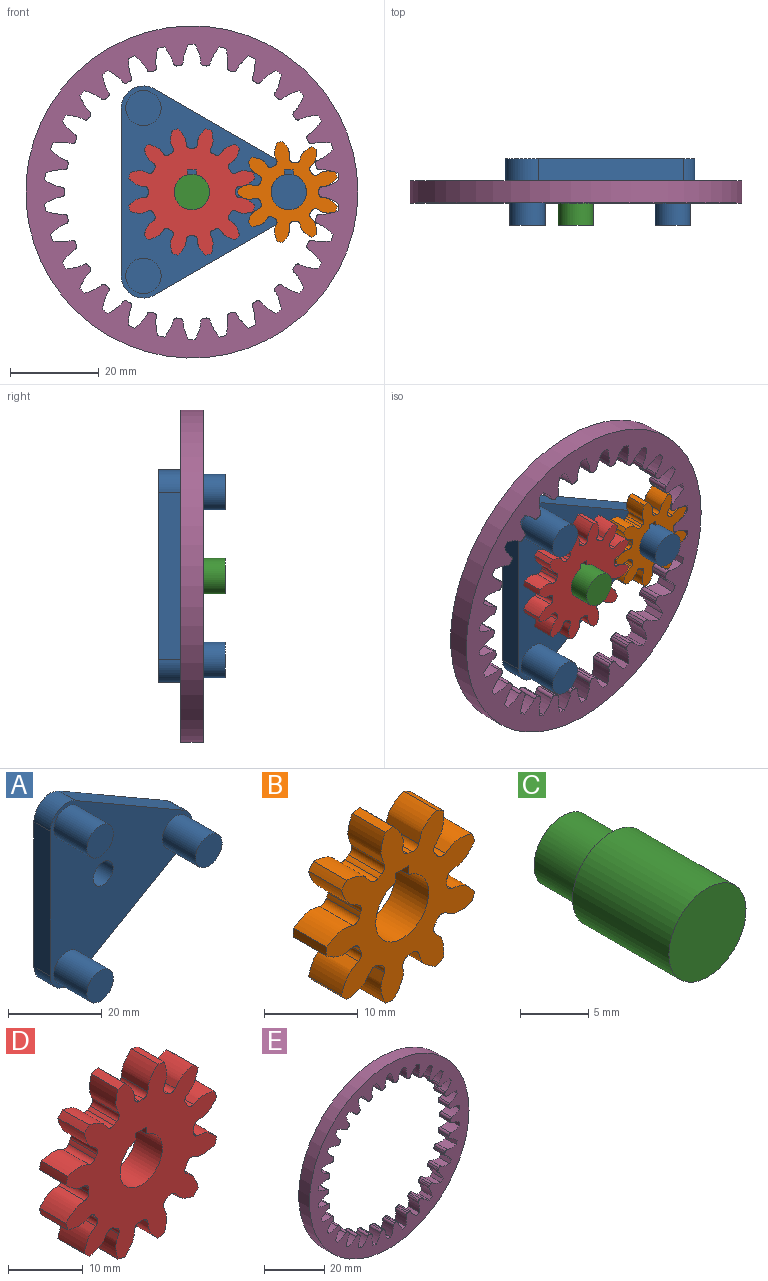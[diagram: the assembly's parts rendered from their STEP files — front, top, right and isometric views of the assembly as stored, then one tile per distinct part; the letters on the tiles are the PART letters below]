
ASSEMBLY  parts=5 mates=3
PART A: 15 faces, bbox 42.8x15x47.9 mm
  f0: cylinder r=5mm len=8.66mm, axis (0,-1,0), area 52.4mm2, adj f1,f5,f6,f7
  f1: plane 32.81x18.94mm, normal (0.5,0,0.87), area 189.4mm2, adj f0,f2,f6,f7
  f2: cylinder r=5mm len=7.5mm, axis (0,-1,0), area 52.4mm2, adj f1,f3,f6,f7
  f3: plane 37.89x5mm, normal (-1,0,0), area 189.4mm2, adj f2,f4,f6,f7
  f4: cylinder r=5mm len=7.5mm, axis (0,-1,0), area 52.4mm2, adj f3,f5,f6,f7
  f5: plane 32.81x18.94mm, normal (0.5,0,-0.87), area 189.4mm2, adj f0,f4,f6,f7
  f6: plane 47.89x42.81mm, normal (0,1,0), area 1240.2mm2, adj f0,f1,f2,f3,f4,f5,f14
  f7: plane 47.89x42.81mm, normal (0,-1,0), area 1089.4mm2, adj f0,f1,f2,f3,f4,f5,f8,f10
  f8: cylinder r=4mm len=10mm, axis (0,1,0), area 251.3mm2, adj f7,f9
  f9: plane 8x8mm, normal (0,-1,0), area 50.3mm2, adj f8
  f10: cylinder r=4mm len=10mm, axis (0,1,0), area 251.3mm2, adj f7,f11
  f11: plane 8x8mm, normal (0,-1,0), area 50.3mm2, adj f10
  f12: cylinder r=4mm len=10mm, axis (0,1,0), area 251.3mm2, adj f7,f13
  f13: plane 8x8mm, normal (0,-1,0), area 50.3mm2, adj f12
  f14: cylinder r=3mm len=6mm, axis (0,1,0), area 94.2mm2, adj f6,f7
PART B: 60 faces, bbox 22.5x5x22.8 mm
  f0: cylinder r=11.46mm len=5mm, axis (0,1,0), area 5.9mm2, adj f8,f14,f40,f57
  f1: cylinder r=11.46mm len=5mm, axis (0,1,0), area 5.9mm2, adj f8,f14,f52,f55
  f2: cylinder r=11.46mm len=5mm, axis (0,1,0), area 5.9mm2, adj f8,f14,f30,f47
  f3: cylinder r=11.46mm len=5mm, axis (0,1,0), area 5.9mm2, adj f8,f14,f42,f45
  f4: cylinder r=11.46mm len=5mm, axis (0,1,0), area 5.9mm2, adj f8,f14,f20,f37
  f5: cylinder r=11.46mm len=5mm, axis (0,1,0), area 5.9mm2, adj f8,f14,f32,f35
  f6: cylinder r=11.46mm len=5mm, axis (0,1,0), area 5.9mm2, adj f8,f14,f15,f27
  f7: cylinder r=11.46mm len=5mm, axis (0,1,0), area 5.9mm2, adj f8,f14,f22,f25
  f8: plane 22.83x22.49mm, normal (0,-1,0), area 210.7mm2, adj f0,f1,f2,f3,f4,f5,f6,f7
  f9: plane 5x1.13mm, normal (-1,0,0), area 5.6mm2, adj f8,f10,f12,f14
  f10: cylinder r=4mm len=8mm, axis (0,1,0), area 115.6mm2, adj f8,f9,f11,f14
  f11: plane 5x1.13mm, normal (1,0,0), area 5.6mm2, adj f8,f10,f12,f14
  f12: plane 5x2mm, normal (0,0,-1), area 10mm2, adj f8,f9,f11,f14
  f13: cylinder r=11.46mm len=5mm, axis (0,1,0), area 5.9mm2, adj f8,f14,f17,f50
  f14: plane 22.83x22.49mm, normal (0,1,0), area 210.7mm2, adj f0,f1,f2,f3,f4,f5,f6,f7
  f15: extruded ~5x3.47mm, area 21.3mm2, adj f6,f8,f14,f18
  f16: cylinder r=6.77mm len=5mm, axis (0,1,0), area 3.2mm2, adj f8,f14,f18,f19
  f17: extruded ~5x3.47mm, area 21.3mm2, adj f8,f13,f14,f19
  f18: cylinder r=0.85mm len=5mm, axis (0,1,0), area 6.2mm2, adj f8,f14,f15,f16
  f19: cylinder r=0.85mm len=5mm, axis (0,1,0), area 6.2mm2, adj f8,f14,f16,f17
  f20: extruded ~5x3.8mm, area 21.3mm2, adj f4,f8,f14,f23
  f21: cylinder r=6.77mm len=5mm, axis (0,1,0), area 3.2mm2, adj f8,f14,f23,f24
  f22: extruded ~5x3.05mm, area 21.3mm2, adj f7,f8,f14,f24
  f23: cylinder r=0.85mm len=5mm, axis (0,1,0), area 6.2mm2, adj f8,f14,f20,f21
  f24: cylinder r=0.85mm len=5mm, axis (0,1,0), area 6.2mm2, adj f8,f14,f21,f22
  f25: extruded ~5x3.89mm, area 21.3mm2, adj f7,f8,f14,f28
  f26: cylinder r=6.77mm len=5mm, axis (0,1,0), area 3.2mm2, adj f8,f14,f28,f29
  f27: extruded ~5x4.05mm, area 21.3mm2, adj f6,f8,f14,f29
  f28: cylinder r=0.85mm len=5mm, axis (0,1,0), area 6.2mm2, adj f8,f14,f25,f26
  f29: cylinder r=0.85mm len=5mm, axis (0,1,0), area 6.2mm2, adj f8,f14,f26,f27
  f30: extruded ~5x4mm, area 21.3mm2, adj f2,f8,f14,f33
  f31: cylinder r=6.77mm len=5mm, axis (0,1,0), area 3.2mm2, adj f8,f14,f33,f34
  f32: extruded ~5x3.22mm, area 21.3mm2, adj f5,f8,f14,f34
  f33: cylinder r=0.85mm len=5mm, axis (0,1,0), area 6.2mm2, adj f8,f14,f30,f31
  f34: cylinder r=0.85mm len=5mm, axis (0,1,0), area 6.2mm2, adj f8,f14,f31,f32
  f35: extruded ~5x3.61mm, area 21.3mm2, adj f5,f8,f14,f38
  f36: cylinder r=6.77mm len=5mm, axis (0,1,0), area 3.2mm2, adj f8,f14,f38,f39
  f37: extruded ~5x4.09mm, area 21.3mm2, adj f4,f8,f14,f39
  f38: cylinder r=0.85mm len=5mm, axis (0,1,0), area 6.2mm2, adj f8,f14,f35,f36
  f39: cylinder r=0.85mm len=5mm, axis (0,1,0), area 6.2mm2, adj f8,f14,f36,f37
  f40: extruded ~5x4.09mm, area 21.3mm2, adj f0,f8,f14,f43
  f41: cylinder r=6.77mm len=5mm, axis (0,1,0), area 3.2mm2, adj f8,f14,f43,f44
  f42: extruded ~5x3.61mm, area 21.3mm2, adj f3,f8,f14,f44
  f43: cylinder r=0.85mm len=5mm, axis (0,1,0), area 6.2mm2, adj f8,f14,f40,f41
  f44: cylinder r=0.85mm len=5mm, axis (0,1,0), area 6.2mm2, adj f8,f14,f41,f42
  f45: extruded ~5x3.22mm, area 21.3mm2, adj f3,f8,f14,f48
  f46: cylinder r=6.77mm len=5mm, axis (0,1,0), area 3.2mm2, adj f8,f14,f48,f49
  f47: extruded ~5x4mm, area 21.3mm2, adj f2,f8,f14,f49
  f48: cylinder r=0.85mm len=5mm, axis (0,1,0), area 6.2mm2, adj f8,f14,f45,f46
  f49: cylinder r=0.85mm len=5mm, axis (0,1,0), area 6.2mm2, adj f8,f14,f46,f47
  f50: extruded ~5x4.05mm, area 21.3mm2, adj f8,f13,f14,f53
  f51: cylinder r=6.77mm len=5mm, axis (0,1,0), area 3.2mm2, adj f8,f14,f53,f54
  f52: extruded ~5x3.89mm, area 21.3mm2, adj f1,f8,f14,f54
  f53: cylinder r=0.85mm len=5mm, axis (0,1,0), area 6.2mm2, adj f8,f14,f50,f51
  f54: cylinder r=0.85mm len=5mm, axis (0,1,0), area 6.2mm2, adj f8,f14,f51,f52
  f55: extruded ~5x3.05mm, area 21.3mm2, adj f1,f8,f14,f58
  f56: cylinder r=6.77mm len=5mm, axis (0,1,0), area 3.2mm2, adj f8,f14,f58,f59
  f57: extruded ~5x3.8mm, area 21.3mm2, adj f0,f8,f14,f59
  f58: cylinder r=0.85mm len=5mm, axis (0,1,0), area 6.2mm2, adj f8,f14,f55,f56
  f59: cylinder r=0.85mm len=5mm, axis (0,1,0), area 6.2mm2, adj f8,f14,f56,f57
PART C: 5 faces, bbox 8x15x8 mm
  f0: cylinder r=4mm len=10mm, axis (0,1,0), area 251.3mm2, adj f1,f2
  f1: plane 8x8mm, normal (0,-1,0), area 50.3mm2, adj f0
  f2: plane 8x8mm, normal (0,1,0), area 22mm2, adj f0,f4
  f3: plane 6x6mm, normal (0,1,0), area 28.3mm2, adj f4
  f4: cylinder r=3mm len=6mm, axis (0,-1,0), area 94.2mm2, adj f2,f3
PART D: 78 faces, bbox 28.5x5x28.5 mm
  f0: cylinder r=14.58mm len=5mm, axis (0,1,0), area 6.5mm2, adj f11,f17,f63,f75
  f1: cylinder r=14.58mm len=5mm, axis (0,1,0), area 6.5mm2, adj f11,f17,f70,f73
  f2: cylinder r=14.58mm len=5mm, axis (0,1,0), area 6.5mm2, adj f11,f17,f58,f65
  f3: cylinder r=14.58mm len=5mm, axis (0,1,0), area 6.5mm2, adj f11,f17,f53,f60
  f4: cylinder r=14.58mm len=5mm, axis (0,1,0), area 6.5mm2, adj f11,f17,f48,f55
  f5: cylinder r=14.58mm len=5mm, axis (0,1,0), area 6.5mm2, adj f11,f17,f38,f50
  f6: cylinder r=14.58mm len=5mm, axis (0,1,0), area 6.5mm2, adj f11,f17,f18,f45
  f7: cylinder r=14.58mm len=5mm, axis (0,1,0), area 6.5mm2, adj f11,f17,f40,f43
  f8: cylinder r=14.58mm len=5mm, axis (0,1,0), area 6.5mm2, adj f11,f17,f28,f35
  f9: cylinder r=14.58mm len=5mm, axis (0,1,0), area 6.5mm2, adj f11,f17,f23,f30
  f10: cylinder r=14.58mm len=5mm, axis (0,1,0), area 6.5mm2, adj f11,f17,f25,f68
  f11: plane 28.55x28.55mm, normal (0,-1,0), area 420.5mm2, adj f0,f1,f2,f3,f4,f5,f6,f7
  f12: plane 5x1.13mm, normal (-1,0,0), area 5.6mm2, adj f11,f13,f15,f17
  f13: cylinder r=4mm len=8mm, axis (0,1,0), area 115.6mm2, adj f11,f12,f14,f17
  f14: plane 5x1.13mm, normal (1,0,0), area 5.6mm2, adj f11,f13,f15,f17
  f15: plane 5x2mm, normal (0,0,-1), area 10mm2, adj f11,f12,f14,f17
  f16: cylinder r=14.58mm len=5mm, axis (0,1,0), area 6.5mm2, adj f11,f17,f20,f33
  f17: plane 28.55x28.55mm, normal (0,1,0), area 420.5mm2, adj f0,f1,f2,f3,f4,f5,f6,f7
  f18: extruded ~5x3.59mm, area 21mm2, adj f6,f11,f17,f21
  f19: cylinder r=9.9mm len=5mm, axis (0,1,0), area 3.5mm2, adj f11,f17,f21,f22
  f20: extruded ~5x3.59mm, area 21mm2, adj f11,f16,f17,f22
  f21: cylinder r=0.86mm len=5mm, axis (0,1,0), area 6.4mm2, adj f11,f17,f18,f19
  f22: cylinder r=0.86mm len=5mm, axis (0,1,0), area 6.4mm2, adj f11,f17,f19,f20
  f23: extruded ~5x3.59mm, area 21mm2, adj f9,f11,f17,f26
  f24: cylinder r=9.9mm len=5mm, axis (0,1,0), area 3.5mm2, adj f11,f17,f26,f27
  f25: extruded ~5x3.59mm, area 21mm2, adj f10,f11,f17,f27
  f26: cylinder r=0.86mm len=5mm, axis (0,1,0), area 6.4mm2, adj f11,f17,f23,f24
  f27: cylinder r=0.86mm len=5mm, axis (0,1,0), area 6.4mm2, adj f11,f17,f24,f25
  f28: extruded ~5x3.45mm, area 21mm2, adj f8,f11,f17,f31
  f29: cylinder r=9.9mm len=5mm, axis (0,1,0), area 3.5mm2, adj f11,f17,f31,f32
  f30: extruded ~5x4.06mm, area 21mm2, adj f9,f11,f17,f32
  f31: cylinder r=0.86mm len=5mm, axis (0,1,0), area 6.4mm2, adj f11,f17,f28,f29
  f32: cylinder r=0.86mm len=5mm, axis (0,1,0), area 6.4mm2, adj f11,f17,f29,f30
  f33: extruded ~5x4.06mm, area 21mm2, adj f11,f16,f17,f36
  f34: cylinder r=9.9mm len=5mm, axis (0,1,0), area 3.5mm2, adj f11,f17,f36,f37
  f35: extruded ~5x3.45mm, area 21mm2, adj f8,f11,f17,f37
  f36: cylinder r=0.86mm len=5mm, axis (0,1,0), area 6.4mm2, adj f11,f17,f33,f34
  f37: cylinder r=0.86mm len=5mm, axis (0,1,0), area 6.4mm2, adj f11,f17,f34,f35
  f38: extruded ~5x4.06mm, area 21mm2, adj f5,f11,f17,f41
  f39: cylinder r=9.9mm len=5mm, axis (0,1,0), area 3.5mm2, adj f11,f17,f41,f42
  f40: extruded ~5x3.45mm, area 21mm2, adj f7,f11,f17,f42
  f41: cylinder r=0.86mm len=5mm, axis (0,1,0), area 6.4mm2, adj f11,f17,f38,f39
  f42: cylinder r=0.86mm len=5mm, axis (0,1,0), area 6.4mm2, adj f11,f17,f39,f40
  f43: extruded ~5x3.45mm, area 21mm2, adj f7,f11,f17,f46
  f44: cylinder r=9.9mm len=5mm, axis (0,1,0), area 3.5mm2, adj f11,f17,f46,f47
  f45: extruded ~5x4.06mm, area 21mm2, adj f6,f11,f17,f47
  f46: cylinder r=0.86mm len=5mm, axis (0,1,0), area 6.4mm2, adj f11,f17,f43,f44
  f47: cylinder r=0.86mm len=5mm, axis (0,1,0), area 6.4mm2, adj f11,f17,f44,f45
  f48: extruded ~5x3.59mm, area 21mm2, adj f4,f11,f17,f51
  f49: cylinder r=9.9mm len=5mm, axis (0,1,0), area 3.5mm2, adj f11,f17,f51,f52
  f50: extruded ~5x3.59mm, area 21mm2, adj f5,f11,f17,f52
  f51: cylinder r=0.86mm len=5mm, axis (0,1,0), area 6.4mm2, adj f11,f17,f48,f49
  f52: cylinder r=0.86mm len=5mm, axis (0,1,0), area 6.4mm2, adj f11,f17,f49,f50
  f53: extruded ~5x3.45mm, area 21mm2, adj f3,f11,f17,f56
  f54: cylinder r=9.9mm len=5mm, axis (0,1,0), area 3.5mm2, adj f11,f17,f56,f57
  f55: extruded ~5x4.06mm, area 21mm2, adj f4,f11,f17,f57
  f56: cylinder r=0.86mm len=5mm, axis (0,1,0), area 6.4mm2, adj f11,f17,f53,f54
  f57: cylinder r=0.86mm len=5mm, axis (0,1,0), area 6.4mm2, adj f11,f17,f54,f55
  f58: extruded ~5x4.06mm, area 21mm2, adj f2,f11,f17,f61
  f59: cylinder r=9.9mm len=5mm, axis (0,1,0), area 3.5mm2, adj f11,f17,f61,f62
  f60: extruded ~5x3.45mm, area 21mm2, adj f3,f11,f17,f62
  f61: cylinder r=0.86mm len=5mm, axis (0,1,0), area 6.4mm2, adj f11,f17,f58,f59
  f62: cylinder r=0.86mm len=5mm, axis (0,1,0), area 6.4mm2, adj f11,f17,f59,f60
  f63: extruded ~5x3.59mm, area 21mm2, adj f0,f11,f17,f66
  f64: cylinder r=9.9mm len=5mm, axis (0,1,0), area 3.5mm2, adj f11,f17,f66,f67
  f65: extruded ~5x3.59mm, area 21mm2, adj f2,f11,f17,f67
  f66: cylinder r=0.86mm len=5mm, axis (0,1,0), area 6.4mm2, adj f11,f17,f63,f64
  f67: cylinder r=0.86mm len=5mm, axis (0,1,0), area 6.4mm2, adj f11,f17,f64,f65
  f68: extruded ~5x4.06mm, area 21mm2, adj f10,f11,f17,f71
  f69: cylinder r=9.9mm len=5mm, axis (0,1,0), area 3.5mm2, adj f11,f17,f71,f72
  f70: extruded ~5x3.45mm, area 21mm2, adj f1,f11,f17,f72
  f71: cylinder r=0.86mm len=5mm, axis (0,1,0), area 6.4mm2, adj f11,f17,f68,f69
  f72: cylinder r=0.86mm len=5mm, axis (0,1,0), area 6.4mm2, adj f11,f17,f69,f70
  f73: extruded ~5x3.45mm, area 21mm2, adj f1,f11,f17,f76
  f74: cylinder r=9.9mm len=5mm, axis (0,1,0), area 3.5mm2, adj f11,f17,f76,f77
  f75: extruded ~5x4.06mm, area 21mm2, adj f0,f11,f17,f77
  f76: cylinder r=0.86mm len=5mm, axis (0,1,0), area 6.4mm2, adj f11,f17,f73,f74
  f77: cylinder r=0.86mm len=5mm, axis (0,1,0), area 6.4mm2, adj f11,f17,f74,f75
PART E: 183 faces, bbox 75x5x75 mm
  f0: plane 75x75mm, normal (0,-1,0), area 1384.2mm2, adj f2,f3,f4,f5,f6,f7,f8,f9
  f1: plane 75x75mm, normal (0,1,0), area 1384.2mm2, adj f2,f3,f4,f5,f6,f7,f8,f9
  f2: cylinder r=37.5mm len=75mm, axis (0,1,0), area 1178.1mm2, adj f0,f1
  f3: cylinder r=33.33mm len=5mm, axis (0,1,0), area 7.7mm2, adj f0,f1,f173,f180
  f4: cylinder r=33.33mm len=5mm, axis (0,1,0), area 7.7mm2, adj f0,f1,f168,f175
  f5: cylinder r=33.33mm len=5mm, axis (0,1,0), area 7.7mm2, adj f0,f1,f163,f170
  f6: cylinder r=33.33mm len=5mm, axis (0,1,0), area 7.7mm2, adj f0,f1,f153,f165
  f7: cylinder r=33.33mm len=5mm, axis (0,1,0), area 7.7mm2, adj f0,f1,f148,f160
  f8: cylinder r=33.33mm len=5mm, axis (0,1,0), area 7.7mm2, adj f0,f1,f155,f158
  f9: cylinder r=33.33mm len=5mm, axis (0,1,0), area 7.7mm2, adj f0,f1,f143,f150
  f10: cylinder r=33.33mm len=5mm, axis (0,1,0), area 7.7mm2, adj f0,f1,f33,f145
  f11: cylinder r=33.33mm len=5mm, axis (0,1,0), area 7.7mm2, adj f0,f1,f128,f140
  f12: cylinder r=33.33mm len=5mm, axis (0,1,0), area 7.7mm2, adj f0,f1,f135,f138
  f13: cylinder r=33.33mm len=5mm, axis (0,1,0), area 7.7mm2, adj f0,f1,f123,f130
  f14: cylinder r=33.33mm len=5mm, axis (0,1,0), area 7.7mm2, adj f0,f1,f125,f178
  f15: cylinder r=33.33mm len=5mm, axis (0,1,0), area 7.7mm2, adj f0,f1,f120,f133
  f16: cylinder r=33.33mm len=5mm, axis (0,1,0), area 7.7mm2, adj f0,f1,f115,f118
  f17: cylinder r=33.33mm len=5mm, axis (0,1,0), area 7.7mm2, adj f0,f1,f110,f113
  f18: cylinder r=33.33mm len=5mm, axis (0,1,0), area 7.7mm2, adj f0,f1,f105,f108
  f19: cylinder r=33.33mm len=5mm, axis (0,1,0), area 7.7mm2, adj f0,f1,f88,f100
  f20: cylinder r=33.33mm len=5mm, axis (0,1,0), area 7.7mm2, adj f0,f1,f95,f98
  f21: cylinder r=33.33mm len=5mm, axis (0,1,0), area 7.7mm2, adj f0,f1,f83,f90
  f22: cylinder r=33.33mm len=5mm, axis (0,1,0), area 7.7mm2, adj f0,f1,f85,f103
  f23: cylinder r=33.33mm len=5mm, axis (0,1,0), area 7.7mm2, adj f0,f1,f80,f93
  f24: cylinder r=33.33mm len=5mm, axis (0,1,0), area 7.7mm2, adj f0,f1,f75,f78
  f25: cylinder r=33.33mm len=5mm, axis (0,1,0), area 7.7mm2, adj f0,f1,f70,f73
  f26: cylinder r=33.33mm len=5mm, axis (0,1,0), area 7.7mm2, adj f0,f1,f65,f68
  f27: cylinder r=33.33mm len=5mm, axis (0,1,0), area 7.7mm2, adj f0,f1,f53,f60
  f28: cylinder r=33.33mm len=5mm, axis (0,1,0), area 7.7mm2, adj f0,f1,f43,f55
  f29: cylinder r=33.33mm len=5mm, axis (0,1,0), area 7.7mm2, adj f0,f1,f50,f63
  f30: cylinder r=33.33mm len=5mm, axis (0,1,0), area 7.7mm2, adj f0,f1,f45,f48
  f31: cylinder r=33.33mm len=5mm, axis (0,1,0), area 7.7mm2, adj f0,f1,f40,f58
  f32: cylinder r=33.33mm len=5mm, axis (0,1,0), area 7.7mm2, adj f0,f1,f35,f38
  f33: extruded ~5x3.86mm, area 21.1mm2, adj f0,f1,f10,f36
  f34: cylinder r=28.65mm len=5mm, axis (0,1,0), area 3.3mm2, adj f0,f1,f36,f37
  f35: extruded ~5x3.86mm, area 21.1mm2, adj f0,f1,f32,f37
  f36: cylinder r=0.77mm len=5mm, axis (0,1,0), area 5.8mm2, adj f0,f1,f33,f34
  f37: cylinder r=0.77mm len=5mm, axis (0,1,0), area 5.8mm2, adj f0,f1,f34,f35
  f38: extruded ~5x4.11mm, area 21.1mm2, adj f0,f1,f32,f41
  f39: cylinder r=28.65mm len=5mm, axis (0,1,0), area 3.3mm2, adj f0,f1,f41,f42
  f40: extruded ~5x3.44mm, area 21.1mm2, adj f0,f1,f31,f42
  f41: cylinder r=0.77mm len=5mm, axis (0,1,0), area 5.8mm2, adj f0,f1,f38,f39
  f42: cylinder r=0.77mm len=5mm, axis (0,1,0), area 5.8mm2, adj f0,f1,f39,f40
  f43: extruded ~5x3.79mm, area 21.1mm2, adj f0,f1,f28,f46
  f44: cylinder r=28.65mm len=5mm, axis (0,1,0), area 3.3mm2, adj f0,f1,f46,f47
  f45: extruded ~5x3.95mm, area 21.1mm2, adj f0,f1,f30,f47
  f46: cylinder r=0.77mm len=5mm, axis (0,1,0), area 5.8mm2, adj f0,f1,f43,f44
  f47: cylinder r=0.77mm len=5mm, axis (0,1,0), area 5.8mm2, adj f0,f1,f44,f45
  f48: extruded ~5x3.33mm, area 21.1mm2, adj f0,f1,f30,f51
  f49: cylinder r=28.65mm len=5mm, axis (0,1,0), area 3.3mm2, adj f0,f1,f51,f52
  f50: extruded ~5x4.15mm, area 21.1mm2, adj f0,f1,f29,f52
  f51: cylinder r=0.77mm len=5mm, axis (0,1,0), area 5.8mm2, adj f0,f1,f48,f49
  f52: cylinder r=0.77mm len=5mm, axis (0,1,0), area 5.8mm2, adj f0,f1,f49,f50
  f53: extruded ~5x4.08mm, area 21.1mm2, adj f0,f1,f27,f56
  f54: cylinder r=28.65mm len=5mm, axis (0,1,0), area 3.3mm2, adj f0,f1,f56,f57
  f55: extruded ~5x3.58mm, area 21.1mm2, adj f0,f1,f28,f57
  f56: cylinder r=0.77mm len=5mm, axis (0,1,0), area 5.8mm2, adj f0,f1,f53,f54
  f57: cylinder r=0.77mm len=5mm, axis (0,1,0), area 5.8mm2, adj f0,f1,f54,f55
  f58: extruded ~5x4.19mm, area 21.1mm2, adj f0,f1,f31,f61
  f59: cylinder r=28.65mm len=5mm, axis (0,1,0), area 3.3mm2, adj f0,f1,f61,f62
  f60: extruded ~5x3.05mm, area 21.1mm2, adj f0,f1,f27,f62
  f61: cylinder r=0.77mm len=5mm, axis (0,1,0), area 5.8mm2, adj f0,f1,f58,f59
  f62: cylinder r=0.77mm len=5mm, axis (0,1,0), area 5.8mm2, adj f0,f1,f59,f60
  f63: extruded ~5x3.17mm, area 21.1mm2, adj f0,f1,f29,f66
  f64: cylinder r=28.65mm len=5mm, axis (0,1,0), area 3.3mm2, adj f0,f1,f66,f67
  f65: extruded ~5x4.17mm, area 21.1mm2, adj f0,f1,f26,f67
  f66: cylinder r=0.77mm len=5mm, axis (0,1,0), area 5.8mm2, adj f0,f1,f63,f64
  f67: cylinder r=0.77mm len=5mm, axis (0,1,0), area 5.8mm2, adj f0,f1,f64,f65
  f68: extruded ~5x3.67mm, area 21.1mm2, adj f0,f1,f26,f71
  f69: cylinder r=28.65mm len=5mm, axis (0,1,0), area 3.3mm2, adj f0,f1,f71,f72
  f70: extruded ~5x4.01mm, area 21.1mm2, adj f0,f1,f25,f72
  f71: cylinder r=0.77mm len=5mm, axis (0,1,0), area 5.8mm2, adj f0,f1,f68,f69
  f72: cylinder r=0.77mm len=5mm, axis (0,1,0), area 5.8mm2, adj f0,f1,f69,f70
  f73: extruded ~5x4.01mm, area 21.1mm2, adj f0,f1,f25,f76
  f74: cylinder r=28.65mm len=5mm, axis (0,1,0), area 3.3mm2, adj f0,f1,f76,f77
  f75: extruded ~5x3.67mm, area 21.1mm2, adj f0,f1,f24,f77
  f76: cylinder r=0.77mm len=5mm, axis (0,1,0), area 5.8mm2, adj f0,f1,f73,f74
  f77: cylinder r=0.77mm len=5mm, axis (0,1,0), area 5.8mm2, adj f0,f1,f74,f75
  f78: extruded ~5x4.17mm, area 21.1mm2, adj f0,f1,f24,f81
  f79: cylinder r=28.65mm len=5mm, axis (0,1,0), area 3.3mm2, adj f0,f1,f81,f82
  f80: extruded ~5x3.17mm, area 21.1mm2, adj f0,f1,f23,f82
  f81: cylinder r=0.77mm len=5mm, axis (0,1,0), area 5.8mm2, adj f0,f1,f78,f79
  f82: cylinder r=0.77mm len=5mm, axis (0,1,0), area 5.8mm2, adj f0,f1,f79,f80
  f83: extruded ~5x3.05mm, area 21.1mm2, adj f0,f1,f21,f86
  f84: cylinder r=28.65mm len=5mm, axis (0,1,0), area 3.3mm2, adj f0,f1,f86,f87
  f85: extruded ~5x4.19mm, area 21.1mm2, adj f0,f1,f22,f87
  f86: cylinder r=0.77mm len=5mm, axis (0,1,0), area 5.8mm2, adj f0,f1,f83,f84
  f87: cylinder r=0.77mm len=5mm, axis (0,1,0), area 5.8mm2, adj f0,f1,f84,f85
  f88: extruded ~5x3.58mm, area 21.1mm2, adj f0,f1,f19,f91
  f89: cylinder r=28.65mm len=5mm, axis (0,1,0), area 3.3mm2, adj f0,f1,f91,f92
  f90: extruded ~5x4.08mm, area 21.1mm2, adj f0,f1,f21,f92
  f91: cylinder r=0.77mm len=5mm, axis (0,1,0), area 5.8mm2, adj f0,f1,f88,f89
  f92: cylinder r=0.77mm len=5mm, axis (0,1,0), area 5.8mm2, adj f0,f1,f89,f90
  f93: extruded ~5x4.15mm, area 21.1mm2, adj f0,f1,f23,f96
  f94: cylinder r=28.65mm len=5mm, axis (0,1,0), area 3.3mm2, adj f0,f1,f96,f97
  f95: extruded ~5x3.33mm, area 21.1mm2, adj f0,f1,f20,f97
  f96: cylinder r=0.77mm len=5mm, axis (0,1,0), area 5.8mm2, adj f0,f1,f93,f94
  f97: cylinder r=0.77mm len=5mm, axis (0,1,0), area 5.8mm2, adj f0,f1,f94,f95
  f98: extruded ~5x3.95mm, area 21.1mm2, adj f0,f1,f20,f101
  f99: cylinder r=28.65mm len=5mm, axis (0,1,0), area 3.3mm2, adj f0,f1,f101,f102
  f100: extruded ~5x3.79mm, area 21.1mm2, adj f0,f1,f19,f102
  f101: cylinder r=0.77mm len=5mm, axis (0,1,0), area 5.8mm2, adj f0,f1,f98,f99
  f102: cylinder r=0.77mm len=5mm, axis (0,1,0), area 5.8mm2, adj f0,f1,f99,f100
  f103: extruded ~5x3.44mm, area 21.1mm2, adj f0,f1,f22,f106
  f104: cylinder r=28.65mm len=5mm, axis (0,1,0), area 3.3mm2, adj f0,f1,f106,f107
  f105: extruded ~5x4.11mm, area 21.1mm2, adj f0,f1,f18,f107
  f106: cylinder r=0.77mm len=5mm, axis (0,1,0), area 5.8mm2, adj f0,f1,f103,f104
  f107: cylinder r=0.77mm len=5mm, axis (0,1,0), area 5.8mm2, adj f0,f1,f104,f105
  f108: extruded ~5x3.86mm, area 21.1mm2, adj f0,f1,f18,f111
  f109: cylinder r=28.65mm len=5mm, axis (0,1,0), area 3.3mm2, adj f0,f1,f111,f112
  f110: extruded ~5x3.86mm, area 21.1mm2, adj f0,f1,f17,f112
  f111: cylinder r=0.77mm len=5mm, axis (0,1,0), area 5.8mm2, adj f0,f1,f108,f109
  f112: cylinder r=0.77mm len=5mm, axis (0,1,0), area 5.8mm2, adj f0,f1,f109,f110
  f113: extruded ~5x4.11mm, area 21.1mm2, adj f0,f1,f17,f116
  f114: cylinder r=28.65mm len=5mm, axis (0,1,0), area 3.3mm2, adj f0,f1,f116,f117
  f115: extruded ~5x3.44mm, area 21.1mm2, adj f0,f1,f16,f117
  f116: cylinder r=0.77mm len=5mm, axis (0,1,0), area 5.8mm2, adj f0,f1,f113,f114
  f117: cylinder r=0.77mm len=5mm, axis (0,1,0), area 5.8mm2, adj f0,f1,f114,f115
  f118: extruded ~5x4.19mm, area 21.1mm2, adj f0,f1,f16,f121
  f119: cylinder r=28.65mm len=5mm, axis (0,1,0), area 3.3mm2, adj f0,f1,f121,f122
  f120: extruded ~5x3.05mm, area 21.1mm2, adj f0,f1,f15,f122
  f121: cylinder r=0.77mm len=5mm, axis (0,1,0), area 5.8mm2, adj f0,f1,f118,f119
  f122: cylinder r=0.77mm len=5mm, axis (0,1,0), area 5.8mm2, adj f0,f1,f119,f120
  f123: extruded ~5x3.17mm, area 21.1mm2, adj f0,f1,f13,f126
  f124: cylinder r=28.65mm len=5mm, axis (0,1,0), area 3.3mm2, adj f0,f1,f126,f127
  f125: extruded ~5x4.17mm, area 21.1mm2, adj f0,f1,f14,f127
  f126: cylinder r=0.77mm len=5mm, axis (0,1,0), area 5.8mm2, adj f0,f1,f123,f124
  f127: cylinder r=0.77mm len=5mm, axis (0,1,0), area 5.8mm2, adj f0,f1,f124,f125
  f128: extruded ~5x3.33mm, area 21.1mm2, adj f0,f1,f11,f131
  f129: cylinder r=28.65mm len=5mm, axis (0,1,0), area 3.3mm2, adj f0,f1,f131,f132
  f130: extruded ~5x4.15mm, area 21.1mm2, adj f0,f1,f13,f132
  f131: cylinder r=0.77mm len=5mm, axis (0,1,0), area 5.8mm2, adj f0,f1,f128,f129
  f132: cylinder r=0.77mm len=5mm, axis (0,1,0), area 5.8mm2, adj f0,f1,f129,f130
  f133: extruded ~5x4.08mm, area 21.1mm2, adj f0,f1,f15,f136
  f134: cylinder r=28.65mm len=5mm, axis (0,1,0), area 3.3mm2, adj f0,f1,f136,f137
  f135: extruded ~5x3.58mm, area 21.1mm2, adj f0,f1,f12,f137
  f136: cylinder r=0.77mm len=5mm, axis (0,1,0), area 5.8mm2, adj f0,f1,f133,f134
  f137: cylinder r=0.77mm len=5mm, axis (0,1,0), area 5.8mm2, adj f0,f1,f134,f135
  f138: extruded ~5x3.79mm, area 21.1mm2, adj f0,f1,f12,f141
  f139: cylinder r=28.65mm len=5mm, axis (0,1,0), area 3.3mm2, adj f0,f1,f141,f142
  f140: extruded ~5x3.95mm, area 21.1mm2, adj f0,f1,f11,f142
  f141: cylinder r=0.77mm len=5mm, axis (0,1,0), area 5.8mm2, adj f0,f1,f138,f139
  f142: cylinder r=0.77mm len=5mm, axis (0,1,0), area 5.8mm2, adj f0,f1,f139,f140
  f143: extruded ~5x3.44mm, area 21.1mm2, adj f0,f1,f9,f146
  f144: cylinder r=28.65mm len=5mm, axis (0,1,0), area 3.3mm2, adj f0,f1,f146,f147
  f145: extruded ~5x4.11mm, area 21.1mm2, adj f0,f1,f10,f147
  f146: cylinder r=0.77mm len=5mm, axis (0,1,0), area 5.8mm2, adj f0,f1,f143,f144
  f147: cylinder r=0.77mm len=5mm, axis (0,1,0), area 5.8mm2, adj f0,f1,f144,f145
  f148: extruded ~5x3.05mm, area 21.1mm2, adj f0,f1,f7,f151
  f149: cylinder r=28.65mm len=5mm, axis (0,1,0), area 3.3mm2, adj f0,f1,f151,f152
  f150: extruded ~5x4.19mm, area 21.1mm2, adj f0,f1,f9,f152
  f151: cylinder r=0.77mm len=5mm, axis (0,1,0), area 5.8mm2, adj f0,f1,f148,f149
  f152: cylinder r=0.77mm len=5mm, axis (0,1,0), area 5.8mm2, adj f0,f1,f149,f150
  f153: extruded ~5x3.95mm, area 21.1mm2, adj f0,f1,f6,f156
  f154: cylinder r=28.65mm len=5mm, axis (0,1,0), area 3.3mm2, adj f0,f1,f156,f157
  f155: extruded ~5x3.79mm, area 21.1mm2, adj f0,f1,f8,f157
  f156: cylinder r=0.77mm len=5mm, axis (0,1,0), area 5.8mm2, adj f0,f1,f153,f154
  f157: cylinder r=0.77mm len=5mm, axis (0,1,0), area 5.8mm2, adj f0,f1,f154,f155
  f158: extruded ~5x3.58mm, area 21.1mm2, adj f0,f1,f8,f161
  f159: cylinder r=28.65mm len=5mm, axis (0,1,0), area 3.3mm2, adj f0,f1,f161,f162
  f160: extruded ~5x4.08mm, area 21.1mm2, adj f0,f1,f7,f162
  f161: cylinder r=0.77mm len=5mm, axis (0,1,0), area 5.8mm2, adj f0,f1,f158,f159
  f162: cylinder r=0.77mm len=5mm, axis (0,1,0), area 5.8mm2, adj f0,f1,f159,f160
  f163: extruded ~5x4.15mm, area 21.1mm2, adj f0,f1,f5,f166
  f164: cylinder r=28.65mm len=5mm, axis (0,1,0), area 3.3mm2, adj f0,f1,f166,f167
  f165: extruded ~5x3.33mm, area 21.1mm2, adj f0,f1,f6,f167
  f166: cylinder r=0.77mm len=5mm, axis (0,1,0), area 5.8mm2, adj f0,f1,f163,f164
  f167: cylinder r=0.77mm len=5mm, axis (0,1,0), area 5.8mm2, adj f0,f1,f164,f165
  f168: extruded ~5x4.17mm, area 21.1mm2, adj f0,f1,f4,f171
  f169: cylinder r=28.65mm len=5mm, axis (0,1,0), area 3.3mm2, adj f0,f1,f171,f172
  f170: extruded ~5x3.17mm, area 21.1mm2, adj f0,f1,f5,f172
  f171: cylinder r=0.77mm len=5mm, axis (0,1,0), area 5.8mm2, adj f0,f1,f168,f169
  f172: cylinder r=0.77mm len=5mm, axis (0,1,0), area 5.8mm2, adj f0,f1,f169,f170
  f173: extruded ~5x4.01mm, area 21.1mm2, adj f0,f1,f3,f176
  f174: cylinder r=28.65mm len=5mm, axis (0,1,0), area 3.3mm2, adj f0,f1,f176,f177
  f175: extruded ~5x3.67mm, area 21.1mm2, adj f0,f1,f4,f177
  f176: cylinder r=0.77mm len=5mm, axis (0,1,0), area 5.8mm2, adj f0,f1,f173,f174
  f177: cylinder r=0.77mm len=5mm, axis (0,1,0), area 5.8mm2, adj f0,f1,f174,f175
  f178: extruded ~5x3.67mm, area 21.1mm2, adj f0,f1,f14,f181
  f179: cylinder r=28.65mm len=5mm, axis (0,1,0), area 3.3mm2, adj f0,f1,f181,f182
  f180: extruded ~5x4.01mm, area 21.1mm2, adj f0,f1,f3,f182
  f181: cylinder r=0.77mm len=5mm, axis (0,1,0), area 5.8mm2, adj f0,f1,f178,f179
  f182: cylinder r=0.77mm len=5mm, axis (0,1,0), area 5.8mm2, adj f0,f1,f179,f180
PLACE A at identity
PLACE B at identity
PLACE C at identity
PLACE D at identity
PLACE E at identity fixed
MATE revolute B.f0 <-> A.f10  axis (0,1,0) through (21.88,0,0)mm
MATE revolute C.f0 <-> E.f2  axis (0,1,0) through (0,0,0)mm
MATE revolute D.f0 <-> C.f0  axis (0,1,0) through (0,0,0)mm
